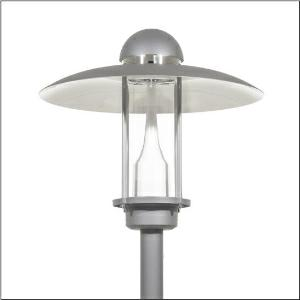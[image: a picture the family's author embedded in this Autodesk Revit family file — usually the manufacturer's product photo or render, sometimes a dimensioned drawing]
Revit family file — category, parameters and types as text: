
# Revit family: city-light_elegance_iq___p1_0a_5xa5265lf14h_79ad
name_source: partatom
category: Lighting Fixtures
units: mm (PartAtom-declared; Revit-internal decimal feet)

## family parameters
Cut with Voids When Loaded = No
Host = Face
Light Source = No
Part Type = Normal
Room Calculation Point = No
Round Connector Dimension = Use Diameter
Shared = No

## types (1)
- --- (1 x LED, 1440 lm, 10 W, 4000K)
    Apparent Load = 10 VA
    CIE Flux Codes = 32 62 91 97 100
    Color Rendering = 70
    Color Temperature = 4000K
    Default Elevation = 1800 mm
    Description = City-Light Elegance iQ, mast luminaire, Module 540 iQ-SR, primary light control with 3 zone facetted reflector, of plastic, silver coated, highly specular, structured, primary optical cover: cover, of PMMA, transparent, light distribution: P1.0a, light emission: direct distribution, primary light characteristic: strongly asymmetric, installation type: post-top, LED, High Power LED, rated luminous flux: 1.440lm, luminous efficacy: 144lm/W, light colour: 740, colour temperature: 4000K, control gear: ECG iQ, control: presetting dimming logarithmic, Street-Remote, Auto-Match, Temp-Guard, Lumen-Switch, Night-Set, Smart-Wire, Light-Fading, Desk-Remote (wireless, voltage-free reading and setting of iQ features in the workshop via application-optimized NFC function/RFID function), optimised constant luminous flux control (CLO 2.0), with terminal, 6-pole, max. 2.5mm², mains connection: 230..240V, AC, 50/60Hz, start of lifetime: 10W, end of service life: 10W, reduction: 5W, luminaire housing, upper part, of aluminium, coated, Siteco® metallic grey (DB 702S), diameter: 750mm, height: 675mm, spigot size: d x l = 76 x 70mm (post-top) | with reducer (optional accessory) 60 x 70mm, post-top mast mounting element, of diecast aluminium, coated, Siteco® metallic grey (DB 702S), Module 540 iQ-SR, traffic white (RAL 9016), equipment: standard, protection rating (complete): IP65, insulation class (complete): insulation class II (safety insulation), certification: CE, ENEC, VDE, packaging unit: 1 piece

Light Distribution: P1.0a
    Height = 675 mm
    Lamp = 1 x LED
    Lamp Light Flux = 1440 lm
    Lamp Power = 10 W
    Lamp count = 1
    Length = 750 mm
    Luminous efficacy = 144 lm/W
    Manufacturer = Siteco
    ModVariant = No
    Model = 5XA5265LF14H
    Number of Poles = 1
    OnlyDefault = Yes
    Power Factor = 1
    Product Name = City-Light Elegance iQ | P1.0a
    Product group = mast luminaire | pylon top
    ProductGroupID = 6100
    Protection Class = Protection class II
    Protection Degree = IP 65
    RLX_Detail_Level = 1
    RLX_Emergency_Light_Flux = 0 lm
    RLX_Emergency_Type = 0
    RLX_Emergency_Type_DB = No
    RlxData = <blob elided: 106249 chars, md5=3bdd6b88>
    Socket = socket
    Standby Power = 0 W
    System Light Flux = 1440 lm
    System Power = 10 W
    Type Comments = factory setting: luminous flux: 100 % | dim-lin: 254 | 401 mA
    Type Image = l_1006912.jpg
    URL = http://relux.com
    VarID = @adj_092017
    Voltage = 0 V
    Weight = 0.00 kg
    Width = 0 mm  [stored 0 ft]

note: [stored X ft] marks values corroborated as IEEE doubles in the binary element streams (Revit-internal decimal feet)

## geometry (parser evidence)
native form markers: Blend x4, Sweep x11
no freeform markers — native parametric forms only
